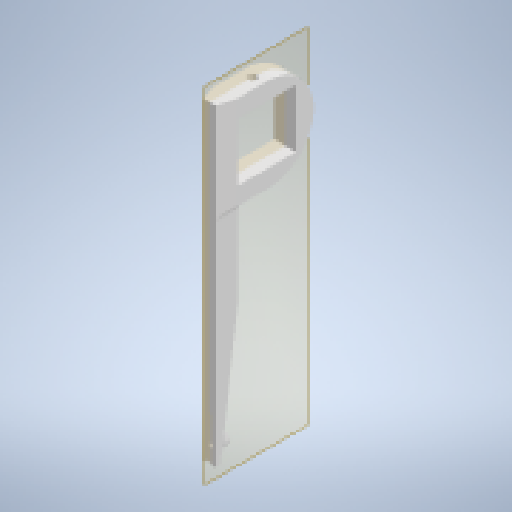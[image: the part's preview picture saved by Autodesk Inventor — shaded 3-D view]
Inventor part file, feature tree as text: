
AUTODESK INVENTOR PART (.ipt)
format: ipt  version: 2023.4 (Build 274418000, 418)  size: 347,648 bytes
history: native  units: mm
features: extrude x6, plane x3, chamfer x2, fillet x2, other x1, sketch x1
ambient origin geometry x8: Origin, YZ Plane, XZ Plane, XY Plane, X Axis, Y Axis, Z Axis, Center Point
bodies: Solid1 (feature_tree)
feature tree (15):
  other  "np2_washing_arm"
  extrude  "Extrusion1"  Depth=21.208mm
  extrude  "Extrusion2"  Depth=5.0mm TaperAngle=0.0deg
  extrude  "Extrusion3"  Depth=50.0mm TaperAngle=0.0deg
  chamfer  "Chamfer1"  Angle=45.0deg  [1 undecoded]
  extrude  "Extrusion4"  TaperAngle=45.0deg  [1 undecoded]
  extrude  "Extrusion5"  Depth=10.0mm TaperAngle=0.0deg
  chamfer  "Chamfer2"  Distance=4.0mm Angle=45.0deg
  plane  "Work Plane1"
  plane  "Work Plane2"
  fillet  "Fillet2"  Radius=1.0mm
  plane  "Work Plane3"
  extrude  "Extrusion8"  Depth=1.0mm
  fillet  "Fillet3"  Radius=5.0mm
  sketch  "Sketch10"  dims[d0=13.208mm d1=21.208mm d2=5.0mm d3=0.0mm d4=50.0mm d5=0.0mm d7=45.0deg d8=45.0deg d11=10.0mm d12=0.0mm d13=4.0mm d14=30.0mm d15=45.0deg d16=1.0mm d17=1.0mm d18=5.0mm d19=0.45mm d21=0.9mm d22=3.5mm d23=10.0mm d24=0.0mm d25=2.5mm d26=3.0mm d27=0.0mm d33=1.0mm d34=3.8mm d35=45.0deg d47=2.0mm d49=1.61mm d50=5.0mm d51=2.5mm d52=1.9mm d53=6.0mm d54=10.0mm d55=0.0mm d56=1.0mm]
note: 2 required parameter values undecoded (feature->parameter linkage not recoverable at this tier; creation-order binding heuristic only, values carry confidence <= 0.55)
